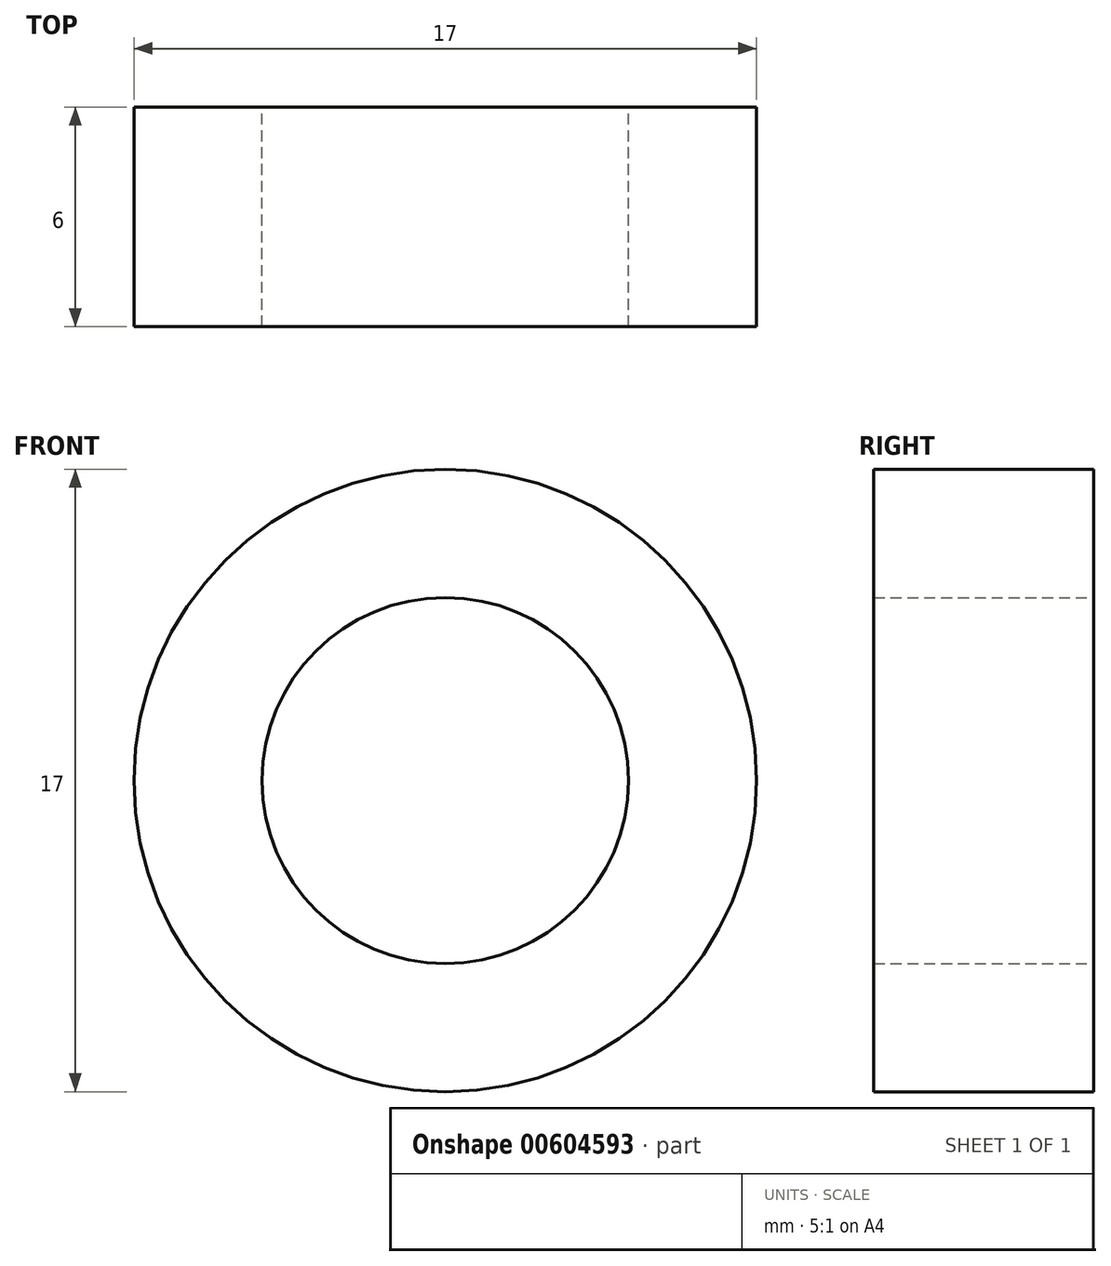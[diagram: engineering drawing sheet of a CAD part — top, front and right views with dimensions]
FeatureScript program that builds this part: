
annotation { "Feature Type Name" : "Feature", "Feature Type Description" : "" }
export const myFeature = defineFeature(function(context is Context, id is Id, definition is map)
    precondition{}
    {
        {
            var Q0;
            Q0=qCreatedBy(makeId("Front.planeOp"),FACE);
            var sketch = newSketch(context, id + "F0", { "sketchPlane" : qUnion([Q0])});
            skCircle(sketch, "E0", {"center": v(0, 0) * mm, "radius": 5 * mm});
            skCircle(sketch, "E1", {"center": v(0, 0) * mm, "radius": 8.5 * mm});
            skSolve(sketch);
        }
        {
            var Q0;
            Q0=makeQuery(id+"F0.imprint","IMPRINT",FACE,{"disambiguationData":[TD([[makeQuery(id+"F0.imprint","IMPRINT",EDGE,{"derivedFrom":sQuery(id+"F0.wireOp",EDGE,"E0")}),-1.0]])]});
            extrude(context, id + "F1", {"entities" : qUnion([Q0]), "depth" : 6 * mm, "offsetDistance" : 25 * mm});
        }
    });
